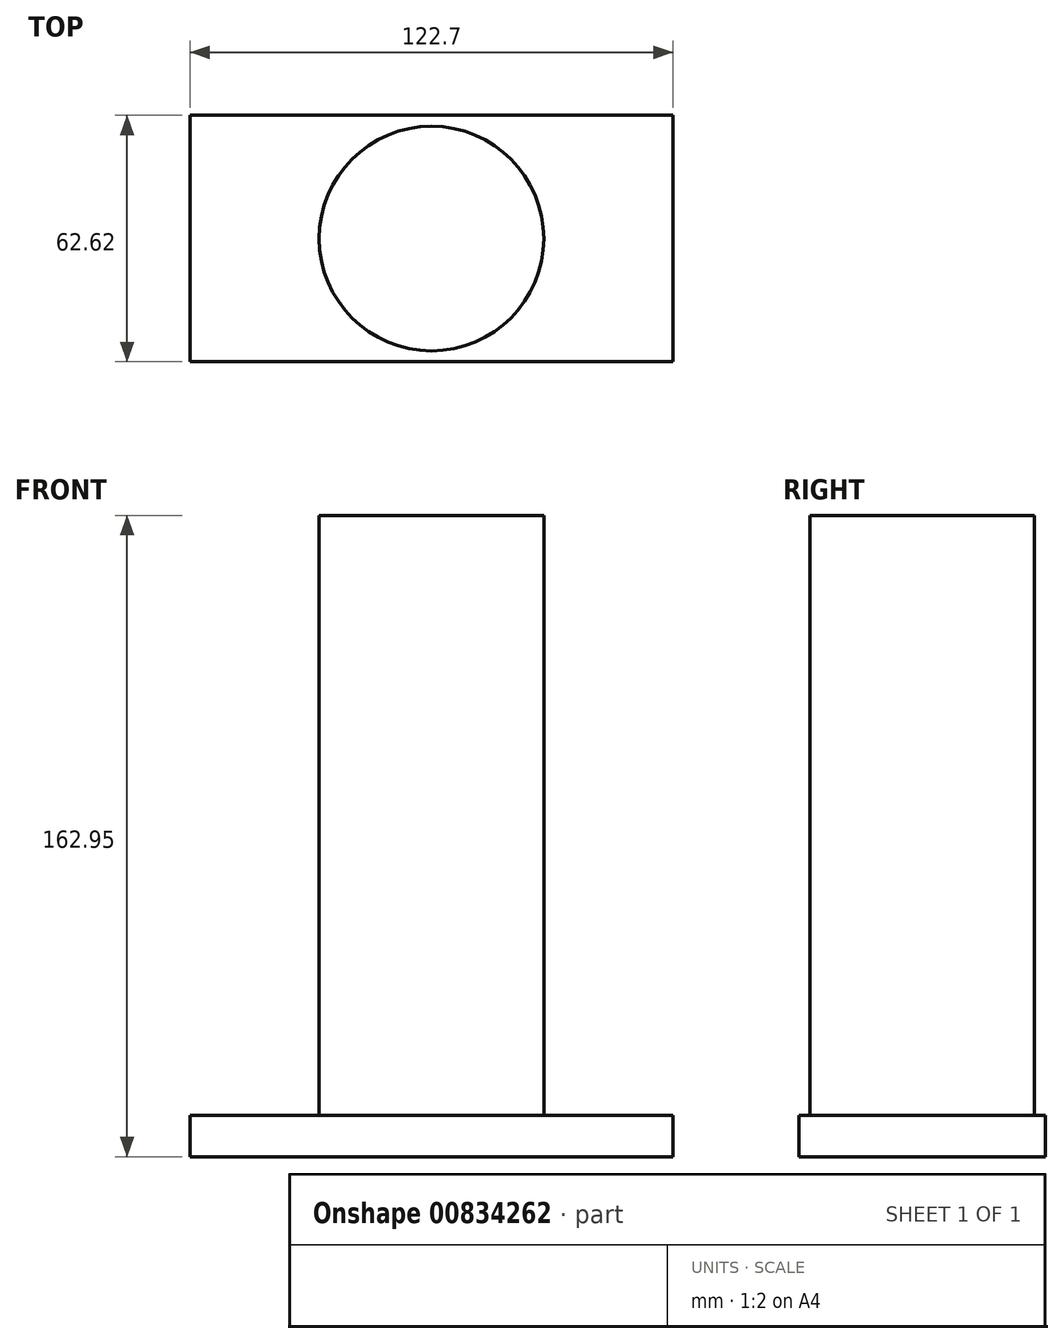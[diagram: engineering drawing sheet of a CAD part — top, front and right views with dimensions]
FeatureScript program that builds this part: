
annotation { "Feature Type Name" : "Feature", "Feature Type Description" : "" }
export const myFeature = defineFeature(function(context is Context, id is Id, definition is map)
    precondition{}
    {
        {
            var Q0;
            Q0=qCreatedBy(makeId("Top.planeOp"),FACE);
            var sketch = newSketch(context, id + "F0", { "sketchPlane" : qUnion([Q0])});
            skCircle(sketch, "E0", {"center": v(0, 0) * mm, "radius": 28.53 * mm});
            skSolve(sketch);
        }
        {
            var Q0;
            Q0 = qSketchRegion(id + "F0", true);
            var Q1;
            Q1=makeQuery(id+"F0.imprint","IMPRINT",FACE,{"disambiguationData":[TD([[makeQuery(id+"F0.imprint","IMPRINT",EDGE,{"derivedFrom":sQuery(id+"F0.wireOp",EDGE,"E0")}),1.0]])]});
            extrude(context, id + "F1", {"entities" : qUnion([Q0, Q1]), "depth" : 152.4 * mm, "offsetDistance" : 25.4 * mm});
        }
        {
            var Q0;
            Q0=qCreatedBy(makeId("Top.planeOp"),FACE);
            var sketch = newSketch(context, id + "F2", { "sketchPlane" : qUnion([Q0])});
            skLineSegment(sketch, "E1.bottom", {"start": v(61.35, -31.3) * mm, "end": v(-61.35, -31.3) * mm});
            skLineSegment(sketch, "E1.top", {"start": v(61.35, 31.3) * mm, "end": v(-61.35, 31.3) * mm});
            skLineSegment(sketch, "E1.left", {"start": v(61.35, -31.3) * mm, "end": v(61.35, 31.3) * mm});
            skLineSegment(sketch, "E1.right", {"start": v(-61.35, -31.3) * mm, "end": v(-61.35, 31.3) * mm});
            skPoint(sketch, "E1.middle", {"position": v(0, 0) * mm});
            skSolve(sketch);
        }
        {
            var Q0;
            Q0=makeQuery(id+"F2.imprint","IMPRINT",FACE,{"disambiguationData":[TD([[makeQuery(id+"F2.imprint","IMPRINT",EDGE,{"derivedFrom":sQuery(id+"F2.wireOp",EDGE,"E1.bottom")}),-1.0]])]});
            extrude(context, id + "F3", {"entities" : qUnion([Q0]), "operationType" : NewBodyOperationType.ADD, "oppositeDirection" : true, "depth" : 10.55 * mm, "offsetDistance" : 25.4 * mm});
        }
    });
